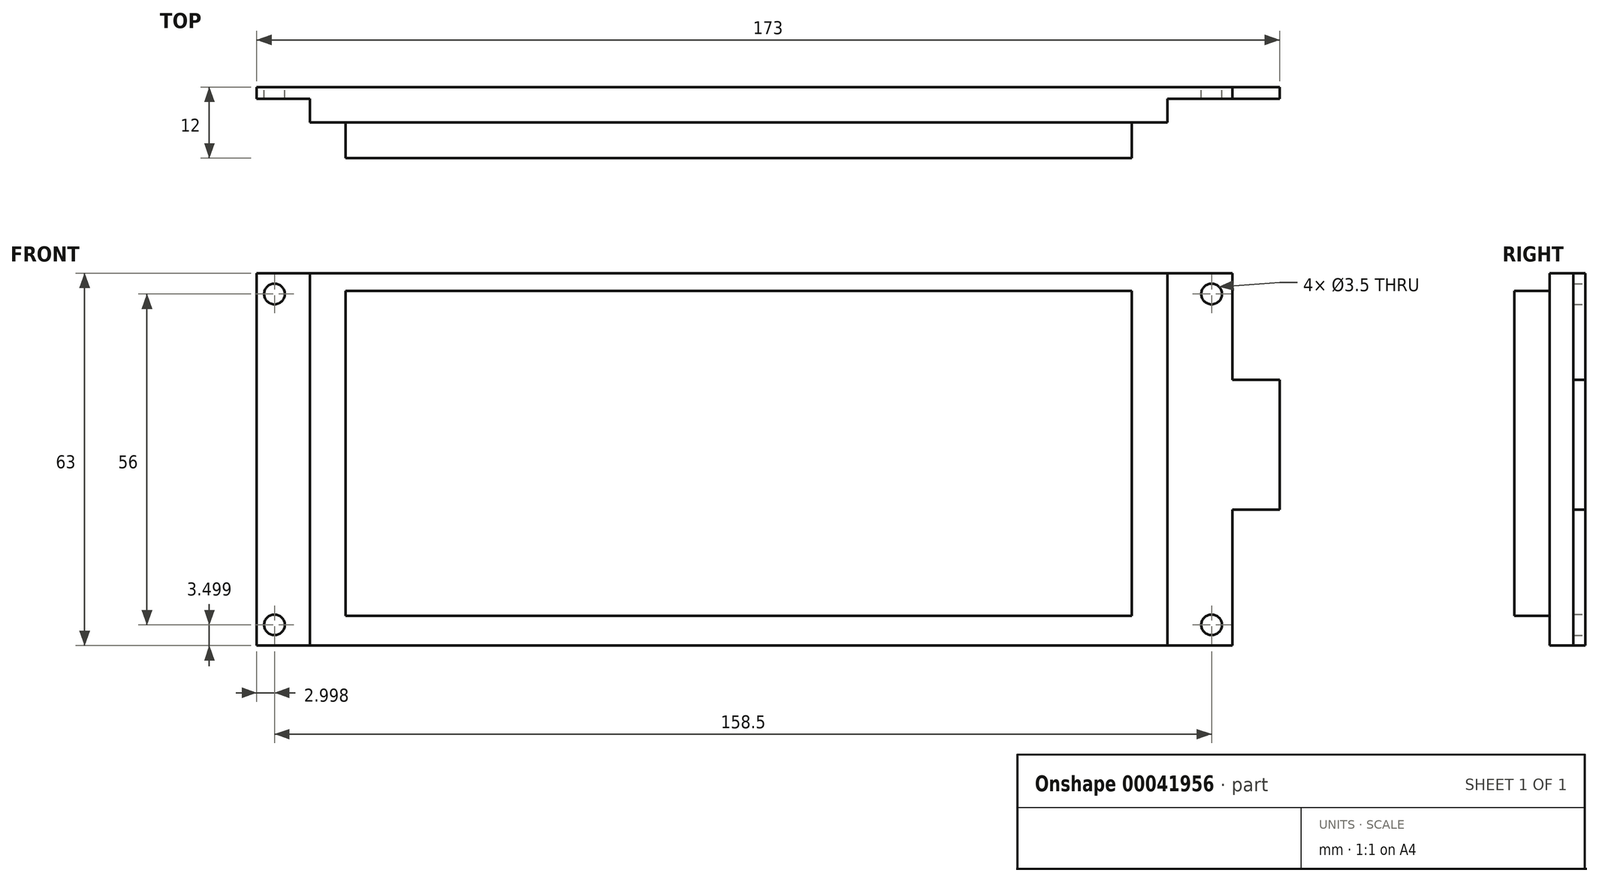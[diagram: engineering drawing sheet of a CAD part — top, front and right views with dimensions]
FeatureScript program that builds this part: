
annotation { "Feature Type Name" : "Feature", "Feature Type Description" : "" }
export const myFeature = defineFeature(function(context is Context, id is Id, definition is map)
    precondition{}
    {
        {
            var Q0;
            Q0=qCreatedBy(makeId("Front.planeOp"),FACE);
            var sketch = newSketch(context, id + "F0", { "sketchPlane" : qUnion([Q0])});
            skLineSegment(sketch, "E0.bottom", {"start": v(-74.91, -41.12) * mm, "end": v(90.09, -41.12) * mm});
            skLineSegment(sketch, "E0.top", {"start": v(-74.91, 21.88) * mm, "end": v(90.09, 21.88) * mm});
            skLineSegment(sketch, "E0.left", {"start": v(-74.91, -41.12) * mm, "end": v(-74.91, 21.88) * mm});
            skLineSegment(sketch, "E0.right", {"start": v(90.09, -41.12) * mm, "end": v(90.09, 21.88) * mm});
            skLineSegment(sketch, "E1", {"start": v(-71.91, 30.78) * mm, "end": v(-71.91, -61.83) * mm});
            skLineSegment(sketch, "E2", {"start": v(86.59, 30.56) * mm, "end": v(86.59, -57.29) * mm});
            skLineSegment(sketch, "E3", {"start": v(-82.54, 18.38) * mm, "end": v(102.47, 18.38) * mm});
            skLineSegment(sketch, "E4", {"start": v(-88.38, -37.62) * mm, "end": v(101.4, -37.62) * mm});
            skPoint(sketch, "E5", {"position": v(-71.91, 18.38) * mm});
            skPoint(sketch, "E6", {"position": v(-71.91, -37.62) * mm});
            skPoint(sketch, "E7", {"position": v(86.59, 18.38) * mm});
            skPoint(sketch, "E8", {"position": v(86.59, -37.62) * mm});
            skSolve(sketch);
        }
        {
            var Q0;
            {var subQ3=sQuery(id+"F0.wireOp",EDGE,"E1");var subQ5=sQuery(id+"F0.wireOp",EDGE,"E3");var subQ7=makeQuery(id+"F0.imprint","INTERSECT",VERTEX,{"derivedFrom":[subQ3,subQ5]});Q0=makeQuery(id+"F0.imprint","IMPRINT",FACE,{"disambiguationData":[TD([[makeQuery(id+"F0.imprint","IMPRINT",EDGE,{"disambiguationData":[TD([[subQ7,-1.0]])],"derivedFrom":subQ3}),1.0]])]});}
            var Q1;
            {var subQ3=sQuery(id+"F0.wireOp",EDGE,"E0.top");var subQ5=sQuery(id+"F0.wireOp",EDGE,"E1");var subQ7=makeQuery(id+"F0.imprint","INTERSECT",VERTEX,{"derivedFrom":[subQ3,subQ5]});Q1=makeQuery(id+"F0.imprint","IMPRINT",FACE,{"disambiguationData":[TD([[makeQuery(id+"F0.imprint","IMPRINT",EDGE,{"disambiguationData":[TD([[subQ7,-1.0]])],"derivedFrom":subQ3}),-1.0]])]});}
            var Q2;
            {var subQ3=sQuery(id+"F0.wireOp",EDGE,"E0.left");var subQ5=sQuery(id+"F0.wireOp",EDGE,"E4");var subQ7=makeQuery(id+"F0.imprint","INTERSECT",VERTEX,{"derivedFrom":[subQ3,subQ5]});Q2=makeQuery(id+"F0.imprint","IMPRINT",FACE,{"disambiguationData":[TD([[makeQuery(id+"F0.imprint","IMPRINT",EDGE,{"disambiguationData":[TD([[subQ7,-1.0]])],"derivedFrom":subQ3}),-1.0]])]});}
            var Q3;
            {var subQ3=sQuery(id+"F0.wireOp",EDGE,"E0.top");var subQ5=sQuery(id+"F0.wireOp",EDGE,"E0.left");var subQ7=makeQuery(id+"F0.imprint","INTERSECT",VERTEX,{"derivedFrom":[subQ3,subQ5]});Q3=makeQuery(id+"F0.imprint","IMPRINT",FACE,{"disambiguationData":[TD([[makeQuery(id+"F0.imprint","IMPRINT",EDGE,{"disambiguationData":[TD([[subQ7,-1.0]])],"derivedFrom":subQ3}),-1.0]])]});}
            var Q4;
            {var subQ3=sQuery(id+"F0.wireOp",EDGE,"E0.bottom");var subQ5=sQuery(id+"F0.wireOp",EDGE,"E0.left");var subQ7=makeQuery(id+"F0.imprint","INTERSECT",VERTEX,{"derivedFrom":[subQ3,subQ5]});Q4=makeQuery(id+"F0.imprint","IMPRINT",FACE,{"disambiguationData":[TD([[makeQuery(id+"F0.imprint","IMPRINT",EDGE,{"disambiguationData":[TD([[subQ7,-1.0]])],"derivedFrom":subQ3}),1.0]])]});}
            var Q5;
            {var subQ3=sQuery(id+"F0.wireOp",EDGE,"E1");var subQ5=sQuery(id+"F0.wireOp",EDGE,"E0.bottom");var subQ6=makeQuery(id+"F0.imprint","INTERSECT",VERTEX,{"derivedFrom":[subQ5,subQ3]});Q5=makeQuery(id+"F0.imprint","IMPRINT",FACE,{"disambiguationData":[TD([[makeQuery(id+"F0.imprint","IMPRINT",EDGE,{"disambiguationData":[TD([[subQ6,-1.0]])],"derivedFrom":subQ5}),1.0]])]});}
            var Q6;
            {var subQ3=sQuery(id+"F0.wireOp",EDGE,"E0.top");var subQ5=sQuery(id+"F0.wireOp",EDGE,"E0.right");var subQ7=makeQuery(id+"F0.imprint","INTERSECT",VERTEX,{"derivedFrom":[subQ3,subQ5]});Q6=makeQuery(id+"F0.imprint","IMPRINT",FACE,{"disambiguationData":[TD([[makeQuery(id+"F0.imprint","IMPRINT",EDGE,{"disambiguationData":[TD([[subQ7,1.0]])],"derivedFrom":subQ3}),-1.0]])]});}
            var Q7;
            {var subQ3=sQuery(id+"F0.wireOp",EDGE,"E0.right");var subQ5=sQuery(id+"F0.wireOp",EDGE,"E4");var subQ7=makeQuery(id+"F0.imprint","INTERSECT",VERTEX,{"derivedFrom":[subQ3,subQ5]});Q7=makeQuery(id+"F0.imprint","IMPRINT",FACE,{"disambiguationData":[TD([[makeQuery(id+"F0.imprint","IMPRINT",EDGE,{"disambiguationData":[TD([[subQ7,-1.0]])],"derivedFrom":subQ3}),1.0]])]});}
            var Q8;
            {var subQ0=sQuery(id+"F0.wireOp",EDGE,"E0.right");var subQ3=sQuery(id+"F0.wireOp",EDGE,"E0.bottom");var subQ4=makeQuery(id+"F0.imprint","INTERSECT",VERTEX,{"derivedFrom":[subQ3,subQ0]});Q8=makeQuery(id+"F0.imprint","IMPRINT",FACE,{"disambiguationData":[TD([[makeQuery(id+"F0.imprint","IMPRINT",EDGE,{"disambiguationData":[TD([[subQ4,1.0]])],"derivedFrom":subQ3}),1.0]])]});}
            extrude(context, id + "F1", {"entities" : qUnion([Q0, Q1, Q2, Q3, Q4, Q5, Q6, Q7, Q8]), "depth" : 2 * mm});
        }
        {
            var Q0;
            Q0=sQuery(id+"F0.wireOp",VERTEX,"E5");
            var Q1;
            Q1=sQuery(id+"F0.wireOp",VERTEX,"E7");
            var Q2;
            Q2=sQuery(id+"F0.wireOp",VERTEX,"E8");
            var Q3;
            Q3=sQuery(id+"F0.wireOp",VERTEX,"E6");
            var Q4;
            Q4=makeQuery(id+"F1.opExtrude","SWEPT_BODY",BODY,{"disambiguationData":[OSD([sQuery(id+"F0.wireOp",EDGE,"E0.bottom"),sQuery(id+"F0.wireOp",EDGE,"E0.top"),sQuery(id+"F0.wireOp",EDGE,"E0.left"),sQuery(id+"F0.wireOp",EDGE,"E0.right")])]});
            hole(context, id + "F2", {"style" : HoleStyle.SIMPLE, "holeDiameter" : 3.5 * mm, "endStyle" : HoleEndStyle.THROUGH, "oppositeDirection" : true, "locations" : qUnion([Q0, Q1, Q2, Q3]), "scope" : qUnion([Q4])});
        }
        {
            var Q0;
            Q0=makeQuery(id+"F1.opExtrude","CAP_FACE",FACE,{"disambiguationData":[OSD([sQuery(id+"F0.wireOp",EDGE,"E0.bottom"),sQuery(id+"F0.wireOp",EDGE,"E0.top"),sQuery(id+"F0.wireOp",EDGE,"E0.left"),sQuery(id+"F0.wireOp",EDGE,"E0.right")])],"isStart":false});
            var sketch = newSketch(context, id + "F3", { "sketchPlane" : qUnion([Q0])});
            skLineSegment(sketch, "E9", {"start": v(79.09, 21.88) * mm, "end": v(79.09, -41.12) * mm});
            skLineSegment(sketch, "E10", {"start": v(-65.91, 21.88) * mm, "end": v(-65.91, -41.12) * mm});
            skSolve(sketch);
        }
        {
            var Q0;
            {var subQ2=sQuery(id+"F3.wireOp",EDGE,"E9");Q0=makeQuery(id+"F3.imprint","IMPRINT",FACE,{"disambiguationData":[TD([[makeQuery(id+"F3.imprint","IMPRINT",EDGE,{"derivedFrom":subQ2}),-1.0]])]});}
            extrude(context, id + "F4", {"entities" : qUnion([Q0]), "operationType" : NewBodyOperationType.ADD, "depth" : 4 * mm});
        }
        {
            var Q0;
            Q0=makeQuery(id+"F1.opExtrude","SWEPT_FACE",FACE,{"disambiguationData":[OSD([sQuery(id+"F0.wireOp",EDGE,"E0.right")])]});
            var sketch = newSketch(context, id + "F5", { "sketchPlane" : qUnion([Q0])});
            skLineSegment(sketch, "E11", {"start": v(-2, 3.88) * mm, "end": v(0, 3.88) * mm});
            skLineSegment(sketch, "E12", {"start": v(-2, -18.12) * mm, "end": v(0, -18.12) * mm});
            skSolve(sketch);
        }
        {
            var Q0;
            {var subQ3=sQuery(id+"F5.wireOp",EDGE,"E11");Q0=makeQuery(id+"F5.imprint","IMPRINT",FACE,{"disambiguationData":[TD([[makeQuery(id+"F5.imprint","IMPRINT",EDGE,{"derivedFrom":subQ3}),-1.0]])]});}
            extrude(context, id + "F6", {"entities" : qUnion([Q0]), "operationType" : NewBodyOperationType.ADD, "depth" : 8 * mm});
        }
        {
            var Q0;
            Q0=makeQuery(id+"F4.opExtrude","CAP_FACE",FACE,{"disambiguationData":[OSD([sQuery(id+"F0.wireOp",EDGE,"E0.bottom"),sQuery(id+"F0.wireOp",EDGE,"E0.top"),sQuery(id+"F3.wireOp",EDGE,"E9"),sQuery(id+"F3.wireOp",EDGE,"E10")])],"isStart":false});
            var sketch = newSketch(context, id + "F7", { "sketchPlane" : qUnion([Q0])});
            skLineSegment(sketch, "E13.bottom", {"start": v(-59.91, -36.12) * mm, "end": v(73.09, -36.12) * mm});
            skLineSegment(sketch, "E13.top", {"start": v(-59.91, 18.88) * mm, "end": v(73.09, 18.88) * mm});
            skLineSegment(sketch, "E13.left", {"start": v(-59.91, -36.12) * mm, "end": v(-59.91, 18.88) * mm});
            skLineSegment(sketch, "E13.right", {"start": v(73.09, -36.12) * mm, "end": v(73.09, 18.88) * mm});
            skSolve(sketch);
        }
        {
            var Q0;
            Q0=makeQuery(id+"F7.imprint","IMPRINT",FACE,{"disambiguationData":[TD([[makeQuery(id+"F7.imprint","IMPRINT",EDGE,{"derivedFrom":sQuery(id+"F7.wireOp",EDGE,"E13.bottom")}),1.0]])]});
            extrude(context, id + "F8", {"entities" : qUnion([Q0]), "operationType" : NewBodyOperationType.ADD, "depth" : 6 * mm});
        }
    });
